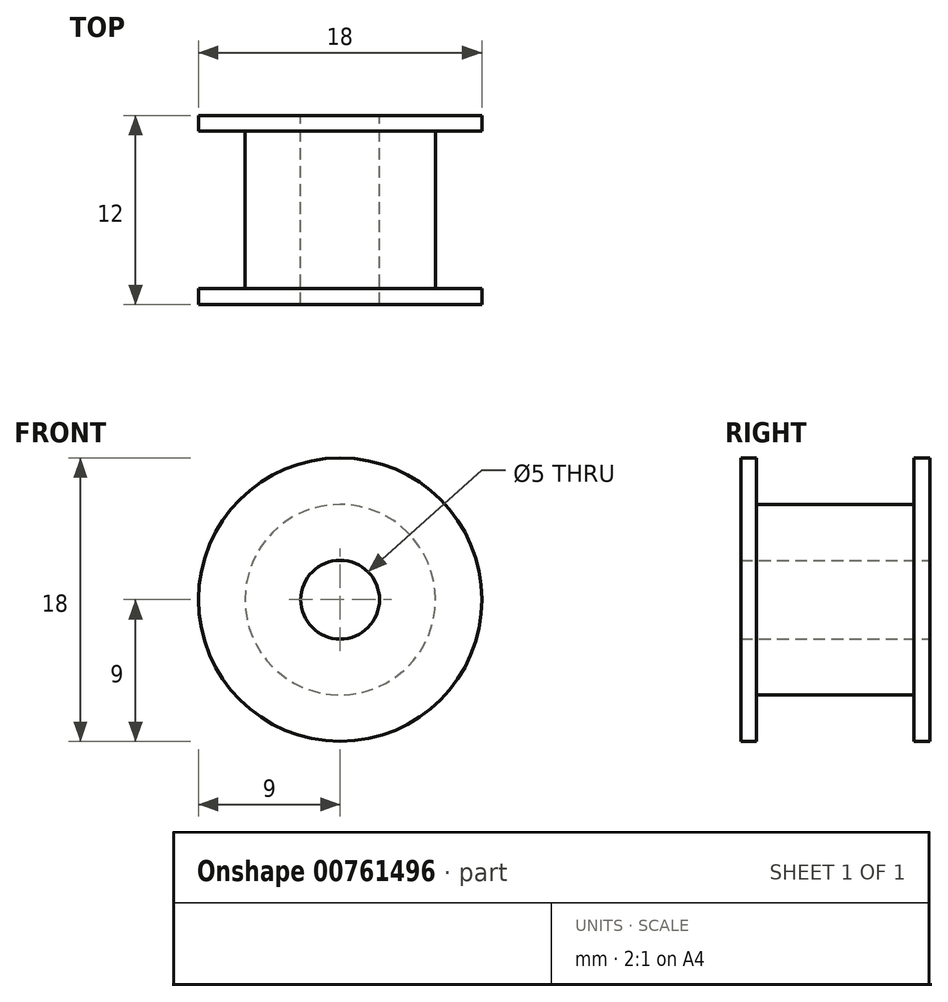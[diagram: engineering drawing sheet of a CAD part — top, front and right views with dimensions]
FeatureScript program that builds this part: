
annotation { "Feature Type Name" : "Feature", "Feature Type Description" : "" }
export const myFeature = defineFeature(function(context is Context, id is Id, definition is map)
    precondition{}
    {
        {
            var Q0;
            Q0=qCreatedBy(makeId("Top.planeOp"),FACE);
            var sketch = newSketch(context, id + "F0", { "sketchPlane" : qUnion([Q0])});
            skLineSegment(sketch, "E0", {"start": v(0, 0) * mm, "end": v(9, 0) * mm});
            skLineSegment(sketch, "E1", {"start": v(9, 0) * mm, "end": v(9, -1) * mm});
            skLineSegment(sketch, "E2", {"start": v(9, -1) * mm, "end": v(6.05, -1) * mm});
            skLineSegment(sketch, "E3", {"start": v(6.05, -1) * mm, "end": v(6.05, -11) * mm});
            skLineSegment(sketch, "E4", {"start": v(6.05, -11) * mm, "end": v(9, -11) * mm});
            skLineSegment(sketch, "E5", {"start": v(9, -11) * mm, "end": v(9, -12) * mm});
            skLineSegment(sketch, "E6", {"start": v(9, -12) * mm, "end": v(0, -12) * mm});
            skLineSegment(sketch, "E7", {"start": v(0, -12) * mm, "end": v(0, 0) * mm});
            skSolve(sketch);
        }
        {
            var Q0;
            Q0 = qSketchRegion(id + "F0", true);
            var Q1;
            Q1=sQuery(id+"F0.wireOp",EDGE,"E7");
            revolve(context, id + "F1", {"surfaceOperationType" : NewSurfaceOperationType.NEW, "entities" : qUnion([Q0]), "axis" : qUnion([Q1]), "revolveType" : RevolveType.FULL});
        }
        {
            var Q0;
            Q0=qCreatedBy(makeId("Front.planeOp"),FACE);
            var sketch = newSketch(context, id + "F2", { "sketchPlane" : qUnion([Q0])});
            skCircle(sketch, "E8", {"center": v(0, 0) * mm, "radius": 2.5 * mm});
            skSolve(sketch);
        }
        {
            var Q0;
            Q0=sQuery(id+"F2.wireOp",VERTEX,"E8.center");
            var Q1;
            Q1=makeQuery(id+"F1.opRevolve","SWEPT_BODY",BODY,{"disambiguationData":[OSD([sQuery(id+"F0.wireOp",EDGE,"E0"),sQuery(id+"F0.wireOp",EDGE,"E1"),sQuery(id+"F0.wireOp",EDGE,"E2"),sQuery(id+"F0.wireOp",EDGE,"E3"),sQuery(id+"F0.wireOp",EDGE,"E4"),sQuery(id+"F0.wireOp",EDGE,"E5"),sQuery(id+"F0.wireOp",EDGE,"E6"),sQuery(id+"F0.wireOp",EDGE,"E7")])]});
            hole(context, id + "F3", {"style" : HoleStyle.SIMPLE, "endStyle" : HoleEndStyle.THROUGH, "oppositeDirection" : true, "holeDiameter" : 5 * mm, "majorDiameter" : 5 * mm, "isTappedThrough" : true, "tappedDepth" : 12 * mm, "tapClearance" : 3, "locations" : qUnion([Q0]), "scope" : qUnion([Q1])});
        }
    });
